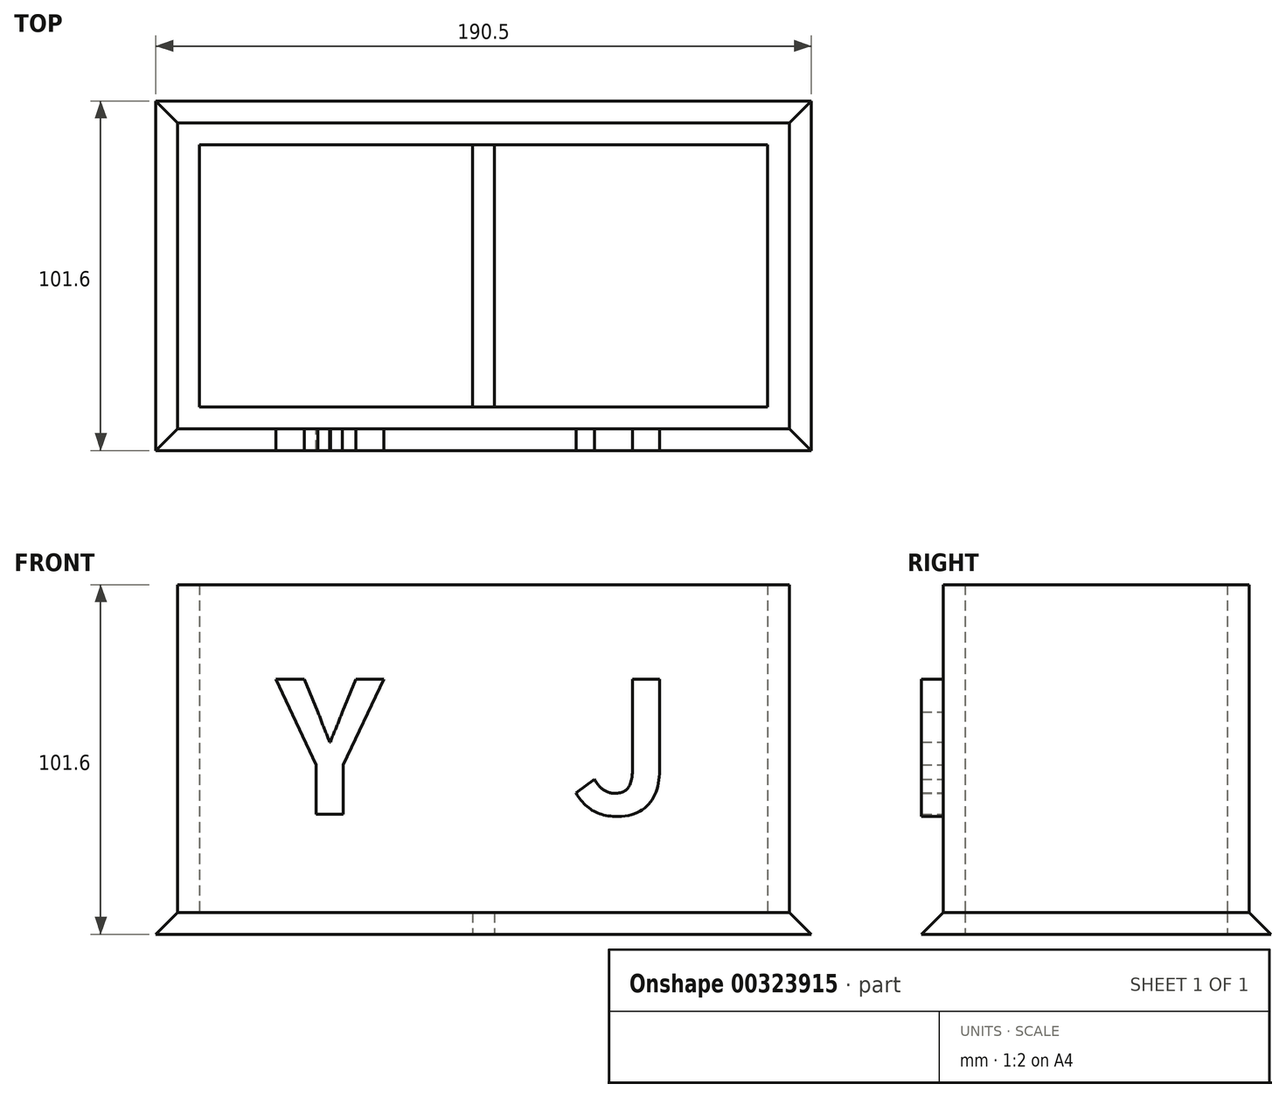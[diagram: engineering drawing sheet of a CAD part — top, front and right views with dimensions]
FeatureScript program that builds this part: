
annotation { "Feature Type Name" : "Feature", "Feature Type Description" : "" }
export const myFeature = defineFeature(function(context is Context, id is Id, definition is map)
    precondition{}
    {
        {
            var Q0;
            Q0=qCreatedBy(makeId("Top.planeOp"),FACE);
            var sketch = newSketch(context, id + "F0", { "sketchPlane" : qUnion([Q0])});
            skLineSegment(sketch, "E0.bottom", {"start": v(82.55, 38.1) * mm, "end": v(-82.55, 38.1) * mm});
            skLineSegment(sketch, "E0.top", {"start": v(82.55, -38.1) * mm, "end": v(-82.55, -38.1) * mm});
            skLineSegment(sketch, "E0.left", {"start": v(82.55, 38.1) * mm, "end": v(82.55, -38.1) * mm});
            skLineSegment(sketch, "E0.right", {"start": v(-82.55, 38.1) * mm, "end": v(-82.55, -38.1) * mm});
            skPoint(sketch, "E0.middle", {"position": v(0, 0) * mm});
            skLineSegment(sketch, "E1.bottom", {"start": v(-3.17, -38.1) * mm, "end": v(3.18, -38.1) * mm});
            skLineSegment(sketch, "E1.top", {"start": v(-3.18, 38.1) * mm, "end": v(3.17, 38.1) * mm});
            skLineSegment(sketch, "E1.left", {"start": v(-3.17, -38.1) * mm, "end": v(-3.18, 38.1) * mm});
            skLineSegment(sketch, "E1.right", {"start": v(3.18, -38.1) * mm, "end": v(3.17, 38.1) * mm});
            skLineSegment(sketch, "E2.0", {"start": v(-88.9, 44.45) * mm, "end": v(-88.9, -44.45) * mm});
            skLineSegment(sketch, "E2.1", {"start": v(88.9, 44.45) * mm, "end": v(-88.9, 44.45) * mm});
            skLineSegment(sketch, "E2.2", {"start": v(88.9, 44.45) * mm, "end": v(88.9, -44.45) * mm});
            skLineSegment(sketch, "E2.3", {"start": v(88.9, -44.45) * mm, "end": v(-88.9, -44.45) * mm});
            skSolve(sketch);
        }
        {
            var Q0;
            Q0 = qSketchRegion(id + "F0", true);
            var Q1;
            Q1=makeQuery(id+"F0.imprint","IMPRINT",FACE,{"disambiguationData":[TD([[makeQuery(id+"F0.imprint","IMPRINT",EDGE,{"derivedFrom":sQuery(id+"F0.wireOp",EDGE,"E1.bottom")}),1.0]])]});
            extrude(context, id + "F1", {"entities" : qUnion([Q0, Q1]), "depth" : 101.6 * mm});
        }
        {
            var Q0;
            {var subQ0=sQuery(id+"F0.wireOp",EDGE,"E0.right");Q0=makeQuery(id+"F0.imprint","IMPRINT",FACE,{"disambiguationData":[TD([[makeQuery(id+"F0.imprint","IMPRINT",EDGE,{"derivedFrom":subQ0}),1.0]])]});}
            var Q1;
            {var subQ0=sQuery(id+"F0.wireOp",EDGE,"E0.left");Q1=makeQuery(id+"F0.imprint","IMPRINT",FACE,{"disambiguationData":[TD([[makeQuery(id+"F0.imprint","IMPRINT",EDGE,{"derivedFrom":subQ0}),-1.0]])]});}
            extrude(context, id + "F2", {"entities" : qUnion([Q0, Q1]), "operationType" : NewBodyOperationType.ADD, "depth" : 6.35 * mm});
        }
        {
            var Q0;
            Q0=qCreatedBy(makeId("Top.planeOp"),FACE);
            var sketch = newSketch(context, id + "F3", { "sketchPlane" : qUnion([Q0])});
            skLineSegment(sketch, "E3.0", {"start": v(88.9, -44.45) * mm, "end": v(-88.9, -44.45) * mm});
            skLineSegment(sketch, "E4.0", {"start": v(88.9, 44.45) * mm, "end": v(88.9, -44.45) * mm});
            skLineSegment(sketch, "E5.0", {"start": v(88.9, 44.45) * mm, "end": v(-88.9, 44.45) * mm});
            skLineSegment(sketch, "E6.0", {"start": v(-88.9, 44.45) * mm, "end": v(-88.9, -44.45) * mm});
            skLineSegment(sketch, "E7.0", {"start": v(-95.25, 50.8) * mm, "end": v(-95.25, -50.8) * mm});
            skLineSegment(sketch, "E7.1", {"start": v(95.25, 50.8) * mm, "end": v(-95.25, 50.8) * mm});
            skLineSegment(sketch, "E7.2", {"start": v(95.25, 50.8) * mm, "end": v(95.25, -50.8) * mm});
            skLineSegment(sketch, "E7.3", {"start": v(95.25, -50.8) * mm, "end": v(-95.25, -50.8) * mm});
            skSolve(sketch);
        }
        {
            var Q0;
            Q0=makeQuery(id+"F3.imprint","IMPRINT",FACE,{"disambiguationData":[TD([[makeQuery(id+"F3.imprint","IMPRINT",EDGE,{"derivedFrom":sQuery(id+"F3.wireOp",EDGE,"E3.0")}),1.0]])]});
            extrude(context, id + "F4", {"entities" : qUnion([Q0]), "operationType" : NewBodyOperationType.ADD, "depth" : 6.35 * mm});
        }
        {
            var Q0;
            Q0=makeQuery(id+"F4.opExtrude","CAP_EDGE",EDGE,{"disambiguationData":[OSD([sQuery(id+"F3.wireOp",EDGE,"E7.3")])],"isStart":false});
            var Q1;
            Q1=makeQuery(id+"F4.opExtrude","CAP_EDGE",EDGE,{"disambiguationData":[OSD([sQuery(id+"F3.wireOp",EDGE,"E7.2")])],"isStart":false});
            var Q2;
            Q2=makeQuery(id+"F4.opExtrude","CAP_EDGE",EDGE,{"disambiguationData":[OSD([sQuery(id+"F3.wireOp",EDGE,"E7.1")])],"isStart":false});
            var Q3;
            Q3=makeQuery(id+"F4.opExtrude","CAP_EDGE",EDGE,{"disambiguationData":[OSD([sQuery(id+"F3.wireOp",EDGE,"E7.0")])],"isStart":false});
            chamfer(context, id + "F5", {"entities" : qUnion([Q0, Q1, Q2, Q3]), "width" : 6.35 * mm, "tangentPropagation" : true});
        }
        {
            var Q0;
            Q0=makeQuery(id+"F1.opExtrude","SWEPT_FACE",FACE,{"disambiguationData":[OSD([sQuery(id+"F0.wireOp",EDGE,"E2.3")])]});
            var sketch = newSketch(context, id + "F6", { "sketchPlane" : qUnion([Q0])});
            skText(sketch, "E8", { "text": "Y", "fontName": "NotoSansCJKsc-Bold.otf"});
            skText(sketch, "E9", { "text": "J", "fontName": "NotoSansCJKsc-Bold.otf"});
            const initialGuessF6  = {"E8": [-0.06005, 0.03493, 1, 0, 0.0381], "E9": [0.02568, 0.03493, 1, 0, 0.0381]};
            skSetInitialGuess(sketch, initialGuessF6);
            skSolve(sketch);
        }
        {
            var Q0;
            Q0 = qSketchRegion(id + "F6", true);
            extrude(context, id + "F7", {"entities" : qUnion([Q0]), "operationType" : NewBodyOperationType.ADD, "depth" : 6.35 * mm});
        }
    });
